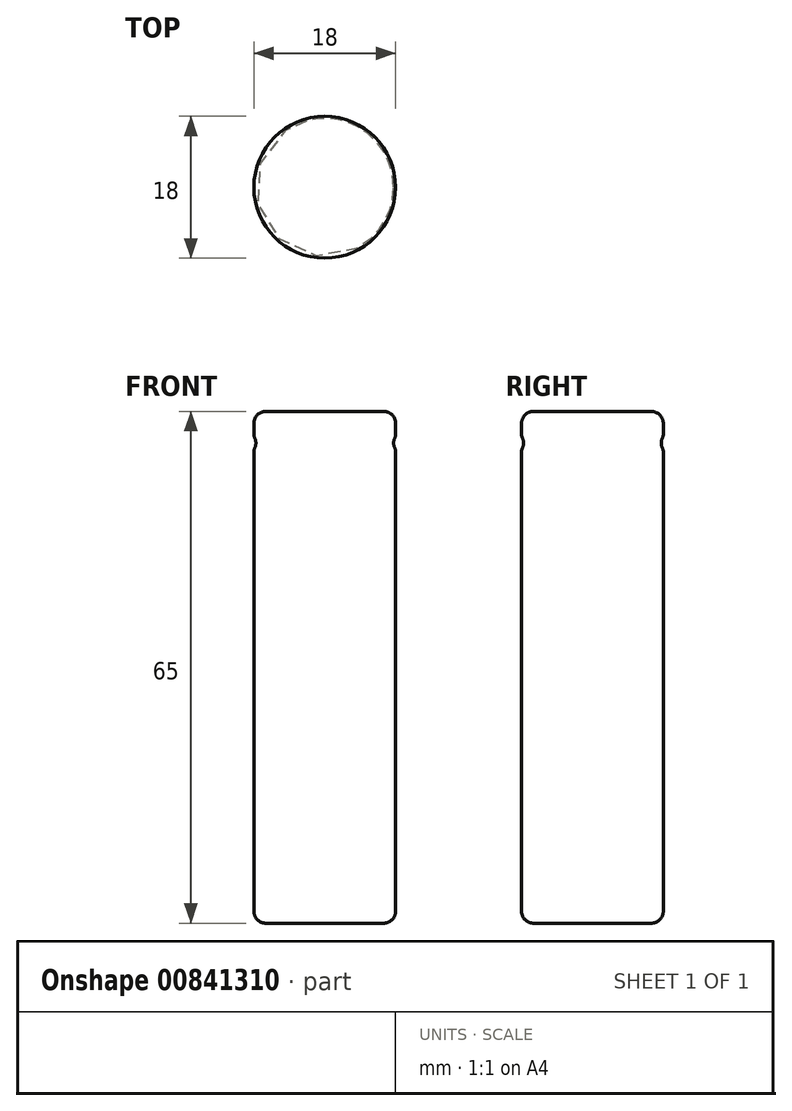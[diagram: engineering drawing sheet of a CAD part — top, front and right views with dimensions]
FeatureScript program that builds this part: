
annotation { "Feature Type Name" : "Feature", "Feature Type Description" : "" }
export const myFeature = defineFeature(function(context is Context, id is Id, definition is map)
    precondition{}
    {
        {
            var Q0;
            Q0=qCreatedBy(makeId("Top.planeOp"),FACE);
            var sketch = newSketch(context, id + "F0", { "sketchPlane" : qUnion([Q0])});
            skCircle(sketch, "E0", {"center": v(0, 0) * mm, "radius": 9 * mm});
            skSolve(sketch);
        }
        {
            var Q0;
            Q0 = qSketchRegion(id + "F0", true);
            extrude(context, id + "F1", {"entities" : qUnion([Q0]), "depth" : 65 * mm, "offsetDistance" : 25.4 * mm});
        }
        {
            var Q0;
            Q0=makeQuery(id+"F1.opExtrude","CAP_EDGE",EDGE,{"disambiguationData":[OSD([sQuery(id+"F0.wireOp",EDGE,"E0")])],"isStart":false});
            var Q1;
            Q1=makeQuery(id+"F1.opExtrude","CAP_EDGE",EDGE,{"disambiguationData":[OSD([sQuery(id+"F0.wireOp",EDGE,"E0")])],"isStart":true});
            fillet(context, id + "F2", {"entities" : qUnion([Q0, Q1]), "radius" : 1.5 * mm, "tangentPropagation" : true, "allowEdgeOverflow" : false});
        }
        {
            var Q0;
            Q0=qCreatedBy(makeId("Front.planeOp"),FACE);
            var sketch = newSketch(context, id + "F3", { "sketchPlane" : qUnion([Q0])});
            skCircle(sketch, "E1", {"center": v(10.25, 61) * mm, "radius": 1.5 * mm});
            skSolve(sketch);
        }
        {
            var Q0;
            Q0=makeQuery(id+"F3.imprint","IMPRINT",FACE,{"disambiguationData":[TD([[makeQuery(id+"F3.imprint","IMPRINT",EDGE,{"derivedFrom":sQuery(id+"F3.wireOp",EDGE,"E1")}),1.0]])]});
            var Q1;
            Q1=sQuery(id+"F3.wireOp",EDGE,"E1");
            var Q2;
            {var subQ0=sQuery(id+"F0.wireOp",EDGE,"E0");Q2=makeQuery(id+"F2.opFillet","BLEND_EDGE",EDGE,{"blendedFrom":[makeQuery(id+"F1.opExtrude","CAP_EDGE",EDGE,{"disambiguationData":[OSD([subQ0])],"isStart":false}),makeQuery(id+"F1.opExtrude","CAP_FACE",FACE,{"disambiguationData":[OSD([subQ0])],"isStart":false})],"blendedInto":[makeQuery(id+"F1.opExtrude","CAP_FACE",FACE,{"disambiguationData":[OSD([subQ0])],"isStart":false})]});}
            revolve(context, id + "F4", {"operationType" : NewBodyOperationType.REMOVE, "surfaceOperationType" : NewSurfaceOperationType.ADD, "entities" : qUnion([Q0]), "surfaceEntities" : qUnion([Q1]), "axis" : qUnion([Q2]), "revolveType" : RevolveType.FULL, "oppositeDirection" : true});
        }
        {
            var Q0;
            Q0=makeQuery(id+"F4.boolean.opBoolean","INTERSECT",EDGE,{"disambiguationData":[OD(1.0)],"derivedFrom":[makeQuery(id+"F1.opExtrude","SWEPT_FACE",FACE,{"disambiguationData":[OSD([sQuery(id+"F0.wireOp",EDGE,"E0")])]}),makeQuery(id+"F4.opRevolve","SWEPT_FACE",FACE,{"disambiguationData":[OSD([sQuery(id+"F3.wireOp",EDGE,"E1")])]})]});
            var Q1;
            Q1=makeQuery(id+"F4.boolean.opBoolean","INTERSECT",EDGE,{"disambiguationData":[OD(0.0)],"derivedFrom":[makeQuery(id+"F1.opExtrude","SWEPT_FACE",FACE,{"disambiguationData":[OSD([sQuery(id+"F0.wireOp",EDGE,"E0")])]}),makeQuery(id+"F4.opRevolve","SWEPT_FACE",FACE,{"disambiguationData":[OSD([sQuery(id+"F3.wireOp",EDGE,"E1")])]})]});
            fillet(context, id + "F5", {"entities" : qUnion([Q0, Q1]), "radius" : 1 * mm, "tangentPropagation" : true, "allowEdgeOverflow" : false});
        }
    });
